FCSTD DOCUMENT  (FreeCAD 0.18.4R)
Label: base-20x40
License: All rights reserved
LicenseURL: http://en.wikipedia.org/wiki/All_rights_reserved
objects: Sketcher::SketchObject×1, PartDesign::Body×1
note: 2 computed .brp shape members not serialized (recipe doc carries the construction recipe); baked Part::Feature solids carry a one-line shape summary decoded from their .brp

FEATURE [Sketcher::SketchObject] Sketch  label="v2040"
  MapMode = 5
  Support = -> [XY_Plane]
  sketch-geometry (78):
    g0: Circle CenterX=-10 CenterY=0 CenterZ=0 NormalX=0 NormalY=0 NormalZ=1 AngleXU=0 Radius=2.5
    g1: Circle CenterX=10 CenterY=0 CenterZ=0 NormalX=0 NormalY=0 NormalZ=1 AngleXU=0 Radius=2.5
    g2: LineSegment StartX=-5.2 StartY=-10 StartZ=0 EndX=5.2 EndY=-10 EndZ=0
    g3: LineSegment StartX=5.2 StartY=-10 StartZ=0 EndX=7 EndY=-8.2 EndZ=0
    g4: LineSegment StartX=7 StartY=-8.2 StartZ=0 EndX=4.9 EndY=-8.2 EndZ=0
    g5: LineSegment StartX=4.9 StartY=-8.2 StartZ=0 EndX=4.9 EndY=-6.1 EndZ=0
    g6: LineSegment StartX=4.9 StartY=-6.1 StartZ=0 EndX=7 EndY=-4 EndZ=0
    g7: LineSegment StartX=7 StartY=-4 StartZ=0 EndX=13 EndY=-4 EndZ=0
    g8: LineSegment StartX=13 StartY=-4 StartZ=0 EndX=15.1 EndY=-6.1 EndZ=0
    g9: LineSegment StartX=15.1 StartY=-6.1 StartZ=0 EndX=15.1 EndY=-8.2 EndZ=0
    g10: LineSegment StartX=15.1 StartY=-8.2 StartZ=0 EndX=13 EndY=-8.2 EndZ=0
    g11: LineSegment StartX=13 StartY=-8.2 StartZ=0 EndX=14.8 EndY=-10 EndZ=0
    g12: LineSegment StartX=14.8 StartY=-10 StartZ=0 EndX=20 EndY=-10 EndZ=0
    g13: LineSegment StartX=20 StartY=-10 StartZ=0 EndX=20 EndY=-4.8 EndZ=0
    g14: LineSegment StartX=20 StartY=-4.8 StartZ=0 EndX=18.2 EndY=-3 EndZ=0
    g15: LineSegment StartX=18.2 StartY=-3 StartZ=0 EndX=18.2 EndY=-5.1 EndZ=0
    g16: LineSegment StartX=18.2 StartY=-5.1 StartZ=0 EndX=16.1 EndY=-5.1 EndZ=0
    g17: LineSegment StartX=16.1 StartY=-5.1 StartZ=0 EndX=14 EndY=-3 EndZ=0
    g18: LineSegment StartX=14 StartY=-3 StartZ=0 EndX=14 EndY=3 EndZ=0
    g19: LineSegment StartX=14 StartY=3 StartZ=0 EndX=16.1 EndY=5.1 EndZ=0
    g20: LineSegment StartX=16.1 StartY=5.1 StartZ=0 EndX=18.2 EndY=5.1 EndZ=0
    g21: LineSegment StartX=18.2 StartY=5.1 StartZ=0 EndX=18.2 EndY=3 EndZ=0
    g22: LineSegment StartX=18.2 StartY=3 StartZ=0 EndX=20 EndY=4.8 EndZ=0
    g23: LineSegment StartX=20 StartY=4.8 StartZ=0 EndX=20 EndY=10 EndZ=0
    g24: LineSegment StartX=20 StartY=10 StartZ=0 EndX=14.8 EndY=10 EndZ=0
    g25: LineSegment StartX=14.8 StartY=10 StartZ=0 EndX=13 EndY=8.2 EndZ=0
    g26: LineSegment StartX=13 StartY=8.2 StartZ=0 EndX=15.1 EndY=8.2 EndZ=0
    g27: LineSegment StartX=15.1 StartY=8.2 StartZ=0 EndX=15.1 EndY=6.1 EndZ=0
    g28: LineSegment StartX=15.1 StartY=6.1 StartZ=0 EndX=13 EndY=4 EndZ=0
    g29: LineSegment StartX=13 StartY=4 StartZ=0 EndX=7 EndY=4 EndZ=0
    g30: LineSegment StartX=7 StartY=4 StartZ=0 EndX=4.9 EndY=6.1 EndZ=0
    g31: LineSegment StartX=4.9 StartY=6.1 StartZ=0 EndX=4.9 EndY=8.2 EndZ=0
    g32: LineSegment StartX=4.9 StartY=8.2 StartZ=0 EndX=7 EndY=8.2 EndZ=0
    g33: LineSegment StartX=7 StartY=8.2 StartZ=0 EndX=5.2 EndY=10 EndZ=0
    g34: LineSegment StartX=5.2 StartY=10 StartZ=0 EndX=-5.2 EndY=10 EndZ=0
    g35: LineSegment StartX=-5.2 StartY=10 StartZ=0 EndX=-7 EndY=8.2 EndZ=0
    g36: LineSegment StartX=-7 StartY=8.2 StartZ=0 EndX=-4.9 EndY=8.2 EndZ=0
    g37: LineSegment StartX=-4.9 StartY=8.2 StartZ=0 EndX=-4.9 EndY=6.1 EndZ=0
    g38: LineSegment StartX=-4.9 StartY=6.1 StartZ=0 EndX=-7 EndY=4 EndZ=0
    g39: LineSegment StartX=-7 StartY=4 StartZ=0 EndX=-13 EndY=4 EndZ=0
    g40: LineSegment StartX=-13 StartY=4 StartZ=0 EndX=-15.1 EndY=6.1 EndZ=0
    g41: LineSegment StartX=-15.1 StartY=6.1 StartZ=0 EndX=-15.1 EndY=8.2 EndZ=0
    g42: LineSegment StartX=-15.1 StartY=8.2 StartZ=0 EndX=-13 EndY=8.2 EndZ=0
    g43: LineSegment StartX=-13 StartY=8.2 StartZ=0 EndX=-14.8 EndY=10 EndZ=0
    g44: LineSegment StartX=-14.8 StartY=10 StartZ=0 EndX=-20 EndY=10 EndZ=0
    g45: LineSegment StartX=-20 StartY=10 StartZ=0 EndX=-20 EndY=4.8 EndZ=0
    g46: LineSegment StartX=-20 StartY=4.8 StartZ=0 EndX=-18.2 EndY=3 EndZ=0
    g47: LineSegment StartX=-18.2 StartY=3 StartZ=0 EndX=-18.2 EndY=5.1 EndZ=0
    g48: LineSegment StartX=-18.2 StartY=5.1 StartZ=0 EndX=-16.1 EndY=5.1 EndZ=0
    g49: LineSegment StartX=-16.1 StartY=5.1 StartZ=0 EndX=-14 EndY=3 EndZ=0
    g50: LineSegment StartX=-14 StartY=3 StartZ=0 EndX=-14 EndY=-3 EndZ=0
    g51: LineSegment StartX=-14 StartY=-3 StartZ=0 EndX=-16.1 EndY=-5.1 EndZ=0
    g52: LineSegment StartX=-16.1 StartY=-5.1 StartZ=0 EndX=-18.2 EndY=-5.1 EndZ=0
    g53: LineSegment StartX=-18.2 StartY=-5.1 StartZ=0 EndX=-18.2 EndY=-3 EndZ=0
    g54: LineSegment StartX=-18.2 StartY=-3 StartZ=0 EndX=-20 EndY=-4.8 EndZ=0
    g55: LineSegment StartX=-20 StartY=-4.8 StartZ=0 EndX=-20 EndY=-10 EndZ=0
    g56: LineSegment StartX=-20 StartY=-10 StartZ=0 EndX=-14.8 EndY=-10 EndZ=0
    g57: LineSegment StartX=-14.8 StartY=-10 StartZ=0 EndX=-13 EndY=-8.2 EndZ=0
    g58: LineSegment StartX=-13 StartY=-8.2 StartZ=0 EndX=-15.1 EndY=-8.2 EndZ=0
    g59: LineSegment StartX=-15.1 StartY=-8.2 StartZ=0 EndX=-15.1 EndY=-6.1 EndZ=0
    g60: LineSegment StartX=-15.1 StartY=-6.1 StartZ=0 EndX=-13 EndY=-4 EndZ=0
    g61: LineSegment StartX=-13 StartY=-4 StartZ=0 EndX=-7 EndY=-4 EndZ=0
    g62: LineSegment StartX=-7 StartY=-4 StartZ=0 EndX=-4.9 EndY=-6.1 EndZ=0
    g63: LineSegment StartX=-4.9 StartY=-6.1 StartZ=0 EndX=-4.9 EndY=-8.2 EndZ=0
    g64: LineSegment StartX=-4.9 StartY=-8.2 StartZ=0 EndX=-7 EndY=-8.2 EndZ=0
    g65: LineSegment StartX=-7 StartY=-8.2 StartZ=0 EndX=-5.2 EndY=-10 EndZ=0
    g66: LineSegment StartX=-2.9 StartY=8.2 StartZ=0 EndX=2.9 EndY=8.2 EndZ=0
    g67: LineSegment StartX=2.9 StartY=8.2 StartZ=0 EndX=2.9 EndY=6.1 EndZ=0
    g68: LineSegment StartX=2.9 StartY=6.1 StartZ=0 EndX=6 EndY=3 EndZ=0
    g69: LineSegment StartX=6 StartY=3 StartZ=0 EndX=6 EndY=-3 EndZ=0
    g70: LineSegment StartX=6 StartY=-3 StartZ=0 EndX=2.9 EndY=-6.1 EndZ=0
    g71: LineSegment StartX=2.9 StartY=-6.1 StartZ=0 EndX=2.9 EndY=-8.2 EndZ=0
    g72: LineSegment StartX=2.9 StartY=-8.2 StartZ=0 EndX=-2.9 EndY=-8.2 EndZ=0
    g73: LineSegment StartX=-2.9 StartY=-8.2 StartZ=0 EndX=-2.9 EndY=-6.1 EndZ=0
    g74: LineSegment StartX=-2.9 StartY=-6.1 StartZ=0 EndX=-6 EndY=-3 EndZ=0
    g75: LineSegment StartX=-6 StartY=-3 StartZ=0 EndX=-6 EndY=3 EndZ=0
    g76: LineSegment StartX=-6 StartY=3 StartZ=0 EndX=-2.9 EndY=6.1 EndZ=0
    g77: LineSegment StartX=-2.9 StartY=6.1 StartZ=0 EndX=-2.9 EndY=8.2 EndZ=0
  constraints (237):
    c: PointOnObject(g0,g-1)
    c: PointOnObject(g1,g-1)
    c: Diameter(g0) = 5
    c: Diameter(g1) = 5
    c: DistanceX(g0,g1) = 20
    c: DistanceX(g0,g-1) = 10
    c: Horizontal(g2)
    c: Coincident(g2,g3)
    c: Coincident(g3,g4)
    c: Horizontal(g4)
    c: Coincident(g4,g5)
    c: Vertical(g5)
    c: Coincident(g5,g6)
    c: Coincident(g6,g7)
    c: Horizontal(g7)
    c: Coincident(g7,g8)
    c: Coincident(g8,g9)
    c: Coincident(g9,g10)
    c: Horizontal(g10)
    c: Coincident(g10,g11)
    c: Coincident(g11,g12)
    c: Horizontal(g12)
    c: Coincident(g12,g13)
    c: Vertical(g13)
    c: Coincident(g13,g14)
    c: Coincident(g14,g15)
    c: Vertical(g15)
    c: Coincident(g15,g16)
    c: Horizontal(g16)
    c: Coincident(g16,g17)
    c: Coincident(g17,g18)
    c: Vertical(g18)
    c: Coincident(g18,g19)
    c: Coincident(g19,g20)
    c: Horizontal(g20)
    c: Coincident(g20,g21)
    c: Coincident(g21,g22)
    c: Coincident(g22,g23)
    c: Vertical(g23)
    c: Coincident(g23,g24)
    c: Horizontal(g24)
    c: Coincident(g24,g25)
    c: Coincident(g25,g26)
    c: Horizontal(g26)
    c: Coincident(g26,g27)
    c: Vertical(g27)
    c: Coincident(g27,g28)
    c: Coincident(g28,g29)
    c: Horizontal(g29)
    c: Coincident(g29,g30)
    c: Coincident(g30,g31)
    c: Vertical(g31)
    c: Coincident(g31,g32)
    c: Horizontal(g32)
    c: Coincident(g32,g33)
    c: Coincident(g33,g34)
    c: Horizontal(g34)
    c: Coincident(g34,g35)
    c: Coincident(g35,g36)
    c: Horizontal(g36)
    c: Coincident(g36,g37)
    c: Vertical(g37)
    c: Coincident(g37,g38)
    c: Coincident(g38,g39)
    c: Horizontal(g39)
    c: Coincident(g39,g40)
    c: Coincident(g40,g41)
    c: Vertical(g41)
    c: Coincident(g41,g42)
    c: Horizontal(g42)
    c: Coincident(g42,g43)
    c: Coincident(g43,g44)
    c: Horizontal(g44)
    c: Coincident(g44,g45)
    c: Vertical(g45)
    c: Coincident(g45,g46)
    c: Coincident(g46,g47)
    c: Vertical(g47)
    c: Coincident(g47,g48)
    c: Horizontal(g48)
    c: Coincident(g48,g49)
    c: Coincident(g49,g50)
    c: Vertical(g50)
    c: Coincident(g50,g51)
    c: Coincident(g51,g52)
    c: Horizontal(g52)
    c: Coincident(g52,g53)
    c: Vertical(g53)
    c: Coincident(g53,g54)
    c: Coincident(g54,g55)
    c: Vertical(g55)
    c: Coincident(g55,g56)
    c: Horizontal(g56)
    c: Coincident(g56,g57)
    c: Coincident(g57,g58)
    c: Horizontal(g58)
    c: Coincident(g58,g59)
    c: Vertical(g59)
    c: Coincident(g59,g60)
    c: Coincident(g60,g61)
    c: Horizontal(g61)
    c: Coincident(g61,g62)
    c: Coincident(g62,g63)
    c: Vertical(g63)
    c: Coincident(g63,g64)
    c: Horizontal(g64)
    c: Coincident(g64,g65)
    c: Coincident(g65,g2)
    c: Vertical(g9)
    c: Equal(g47,g48)
    c: Equal(g53,g52)
    c: Equal(g52,g48)
    c: Equal(g52,g59)
    c: Equal(g58,g59)
    c: Equal(g59,g63)
    c: Equal(g63,g64)
    c: Equal(g63,g5)
    c: Equal(g5,g4)
    c: Equal(g5,g9)
    c: Equal(g9,g10)
    c: Equal(g9,g16)
    c: Equal(g16,g15)
    c: Vertical(g21)
    c: Equal(g20,g21)
    c: Equal(g20,g16)
    c: Equal(g20,g27)
    c: Equal(g26,g27)
    c: Equal(g32,g31)
    c: Equal(g27,g31)
    c: Equal(g36,g37)
    c: Equal(g37,g31)
    c: Equal(g42,g41)
    c: Equal(g42,g36)
    c: Equal(g41,g48)
    c: Equal(g50,g18)
    c: Equal(g29,g7)
    c: Equal(g39,g61)
    c: Equal(g50,g39)
    c: Equal(g61,g7)
    c: Equal(g29,g18)
    c: Equal(g49,g51)
    c: Equal(g49,g40)
    c: Equal(g40,g38)
    c: Equal(g38,g30)
    c: Equal(g30,g28)
    c: Equal(g28,g19)
    c: Equal(g19,g17)
    c: Equal(g17,g8)
    c: Equal(g8,g6)
    c: Equal(g6,g62)
    c: Equal(g62,g60)
    c: Equal(g60,g51)
    c: Equal(g45,g44)
    c: Equal(g45,g55)
    c: Equal(g55,g56)
    c: Equal(g56,g12)
    c: Equal(g12,g13)
    c: Equal(g13,g23)
    c: Equal(g23,g24)
    c: Equal(g34,g2)
    c: Parallel(g49,g40)
    c: Parallel(g51,g60)
    c: Parallel(g8,g17)
    c: Parallel(g19,g28)
    c: Equal(g46,g54)
    c: Equal(g46,g43)
    c: Equal(g43,g35)
    c: Equal(g35,g33)
    c: Equal(g33,g25)
    c: Equal(g25,g22)
    c: Equal(g22,g14)
    c: Equal(g14,g11)
    c: Equal(g11,g3)
    c: Equal(g3,g65)
    c: Equal(g65,g57)
    c: Parallel(g54,g57)
    c: Parallel(g11,g14)
    c: Parallel(g22,g25)
    c: Parallel(g43,g46)
    c: Parallel(g35,g3)
    c: Parallel(g65,g33)
    c: Angle(g35,g43) = 1.5708
    c: Angle(g25,g33) = 1.5708
    c: Angle(g3,g11) = 1.5708
    c: DistanceY(g14,g21) = 6
    c: DistanceY(g53,g46) = 6
    c: DistanceX(g54,g52) = 1.8
    c: DistanceY(g56,g57) = 1.8
    c: Angle(g6,g8) = 1.5708
    c: Angle(g17,g19) = 1.5708
    c: Angle(g28,g30) = 1.5708
    c: DistanceY(g12,g9) = 1.8
    c: Angle(g60,g62) = 1.5708
    c: DistanceX(g54,g50) = 6
    c: DistanceX(g45,g49) = 6
    c: DistanceY(g50,g50) = 6
    c: DistanceY(g55,g44) = 20
    c: DistanceX(g55,g12) = 40
    c: Angle(g57,g65) = 1.5708
    c: DistanceX(g54,g0) = 10
    c: DistanceY(g0,g43) = 10
    c: Horizontal(g66)
    c: Coincident(g66,g67)
    c: Vertical(g67)
    c: Coincident(g67,g68)
    c: Coincident(g68,g69)
    c: Vertical(g69)
    c: Coincident(g69,g70)
    c: Coincident(g70,g71)
    c: Vertical(g71)
    c: Coincident(g71,g72)
    c: Horizontal(g72)
    c: Coincident(g72,g73)
    c: Vertical(g73)
    c: Coincident(g73,g74)
    c: Coincident(g74,g75)
    c: Vertical(g75)
    c: Coincident(g75,g76)
    c: Coincident(g76,g77)
    c: Coincident(g77,g66)
    c: Vertical(g77)
    c: Parallel(g68,g30)
    c: Parallel(g38,g76)
    c: Parallel(g74,g62)
    c: Parallel(g70,g6)
    c: DistanceY(g2,g71) = 1.8
    c: DistanceY(g66,g33) = 1.8
    c: Equal(g37,g77)
    c: Equal(g67,g31)
    c: Equal(g73,g63)
    c: Equal(g71,g5)
    c: DistanceY(g75,g75) = 6
    c: Equal(g75,g69)
    c: DistanceX(g75,g68) = 12
    c: Equal(g76,g70)
    c: Equal(g70,g74)
    c: DistanceX(g54,g74) = 14
FEATURE [PartDesign::Body] Body
  Group = -> [Sketch]
  Origin = -> Origin
